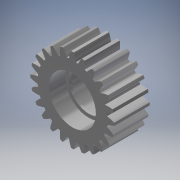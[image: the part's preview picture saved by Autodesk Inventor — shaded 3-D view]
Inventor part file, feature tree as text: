
AUTODESK INVENTOR PART (.ipt)
format: ipt  version: 2019 (Build 230136000, 136)  size: 262,144 bytes
history: native  units: mm (DEFAULTED — no unit token found)
features: sketch x5, extrude x4, plane x3, other x3
ambient origin geometry x8: Origin, YZ Plane, XZ Plane, XY Plane, X Axis, Y Axis, Z Axis, Center Point
bodies: Solid1 (feature_tree)
feature tree (15):
  extrude  "Extrusion1"  Depth=15.0mm TaperAngle=0.0deg
  plane  "Work Plane2"
  plane  "Work Plane8"
  plane  "Work Plane9"
  other  "正齒輪"
  extrude  "擠出2"  Depth=10.0mm TaperAngle=0.0deg
  extrude  "擠出4"  Depth=1.0mm
  extrude  "擠出5"  Depth=1.0mm TaperAngle=0.0deg
  sketch  "Sketch1"  dims[d0=35.714032mm d1=15.0mm d2=0.0mm]
  sketch  "Sketch2"  dims[d3=33.355289mm d4=10.0mm d5=0.0mm d16=43.083915mm d17=0.0mm d34=1.308997mm d39=0.0mm d41=0.0mm d43=43.083915mm d46=43.083915mm d47=0.0mm d48=0.0mm d49=20.0mm d50=7.0mm d51=0.0mm d66=7.0mm d67=0.0mm d68=17.0mm d69=8.0mm d70=3.5mm d71=0.0mm d72=0.0mm d59=1.0mm d60=1.0mm d61=1.0mm d62=0.15mm d63=0.25mm d64=0.375mm d65=14.3117mm]
  other  "Srf1"
  sketch  "草圖3"
  sketch  "草圖7"
  sketch  "草圖8"
  other  "節圓直徑"
